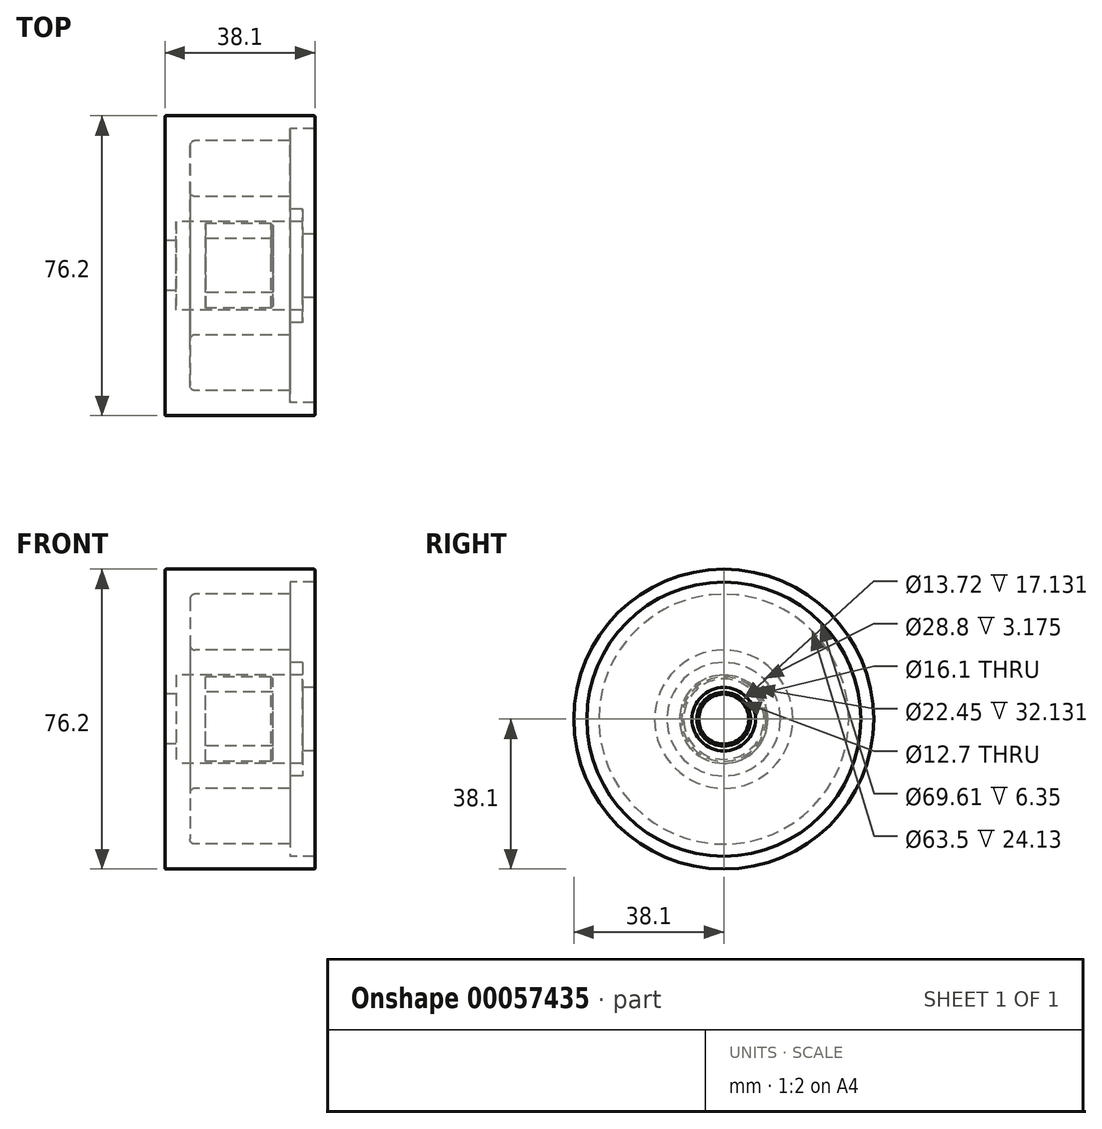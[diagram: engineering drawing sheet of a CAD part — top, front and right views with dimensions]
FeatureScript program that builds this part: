
annotation { "Feature Type Name" : "Feature", "Feature Type Description" : "" }
export const myFeature = defineFeature(function(context is Context, id is Id, definition is map)
    precondition{}
    {
        {
            var Q0;
            Q0=qCreatedBy(makeId("Front.planeOp"),FACE);
            var sketch = newSketch(context, id + "F0", { "sketchPlane" : qUnion([Q0])});
            skLineSegment(sketch, "E0.bottom", {"start": v(0.25, 38.1) * mm, "end": v(37.85, 38.1) * mm});
            skLineSegment(sketch, "E0.left", {"start": v(0, 37.85) * mm, "end": v(0, 6.35) * mm});
            skLineSegment(sketch, "E0.right", {"start": v(38.1, 37.85) * mm, "end": v(38.1, 31.77) * mm});
            skLineSegment(sketch, "E1.bottom", {"start": v(31.75, 31.75) * mm, "end": v(7.62, 31.75) * mm});
            skLineSegment(sketch, "E1.top", {"start": v(31.75, 17.58) * mm, "end": v(7.62, 17.58) * mm});
            skLineSegment(sketch, "E1.right", {"start": v(6.35, 30.48) * mm, "end": v(6.35, 18.85) * mm});
            skLineSegment(sketch, "E2.trimOffspring", {"start": v(38.1, 17.58) * mm, "end": v(38.1, 11.23) * mm});
            skLineSegment(sketch, "E3.bottom", {"start": v(0, 6.35) * mm, "end": v(2.8, 6.35) * mm});
            skLineSegment(sketch, "E4.bottom", {"start": v(38.1, 11.23) * mm, "end": v(2.8, 11.23) * mm});
            skLineSegment(sketch, "E4.right", {"start": v(2.8, 11.23) * mm, "end": v(2.8, 6.35) * mm});
            skPoint(sketch, "E5.visualSharp", {"position": v(0, 38.1) * mm});
            skArc(sketch, "E5.filletArc", {"start": v(0.25, 38.1) * mm, "mid": v(0.07, 38.03) * mm, "end": v(0, 37.85) * mm});
            skPoint(sketch, "E6.visualSharp", {"position": v(38.1, 38.1) * mm});
            skArc(sketch, "E6.filletArc", {"start": v(38.1, 37.85) * mm, "mid": v(38.03, 38.03) * mm, "end": v(37.85, 38.1) * mm});
            skPoint(sketch, "E7.visualSharp", {"position": v(38.1, 31.75) * mm});
            skPoint(sketch, "E8.visualSharp", {"position": v(6.35, 31.75) * mm});
            skArc(sketch, "E8.filletArc", {"start": v(7.62, 31.75) * mm, "mid": v(6.72, 31.38) * mm, "end": v(6.35, 30.48) * mm});
            skPoint(sketch, "E9.visualSharp", {"position": v(6.35, 17.58) * mm});
            skArc(sketch, "E9.filletArc", {"start": v(6.35, 18.85) * mm, "mid": v(6.72, 17.95) * mm, "end": v(7.62, 17.58) * mm});
            skPoint(sketch, "E10.visualSharp", {"position": v(38.1, 17.58) * mm});
            skLineSegment(sketch, "E11", {"start": v(0, 0) * mm, "end": v(46.74, 0) * mm, "construction": true});
            skLineSegment(sketch, "E12.left", {"start": v(38.1, 31.77) * mm, "end": v(38.1, 17.46) * mm});
            skLineSegment(sketch, "E12.right", {"start": v(31.75, 31.75) * mm, "end": v(31.75, 17.58) * mm});
            skPoint(sketch, "E13.visualSharp", {"position": v(31.75, 17.58) * mm});
            skSolve(sketch);
        }
        {
            var Q0;
            Q0=makeQuery(id+"F0.imprint","IMPRINT",FACE,{"disambiguationData":[TD([[makeQuery(id+"F0.imprint","IMPRINT",EDGE,{"derivedFrom":sQuery(id+"F0.wireOp",EDGE,"E0.bottom")}),-1.0]])]});
            var Q1;
            Q1=sQuery(id+"F0.wireOp",EDGE,"E11");
            revolve(context, id + "F1", {"entities" : qUnion([Q0]), "axis" : qUnion([Q1]), "revolveType" : RevolveType.FULL});
        }
        {
            var Q0;
            Q0=qCreatedBy(makeId("Front.planeOp"),FACE);
            var sketch = newSketch(context, id + "F2", { "sketchPlane" : qUnion([Q0])});
            skLineSegment(sketch, "E14.0", {"start": v(38.1, 37.85) * mm, "end": v(38.1, 31.77) * mm, "construction": true});
            skLineSegment(sketch, "E15.0", {"start": v(31.75, 31.75) * mm, "end": v(31.75, 17.58) * mm, "construction": true});
            skLineSegment(sketch, "E16.0", {"start": v(38.1, 17.58) * mm, "end": v(38.1, 11.23) * mm, "construction": true});
            skLineSegment(sketch, "E17.bottom", {"start": v(38.1, 34.8) * mm, "end": v(31.75, 34.8) * mm});
            skLineSegment(sketch, "E17.top", {"start": v(34.93, 14.4) * mm, "end": v(31.75, 14.4) * mm});
            skLineSegment(sketch, "E17.left", {"start": v(38.1, 34.8) * mm, "end": v(38.1, 14.4) * mm});
            skLineSegment(sketch, "E17.right", {"start": v(31.75, 34.8) * mm, "end": v(31.75, 14.4) * mm});
            skLineSegment(sketch, "E18.top", {"start": v(38.1, 8.05) * mm, "end": v(34.93, 8.05) * mm});
            skLineSegment(sketch, "E18.left", {"start": v(38.1, 11.23) * mm, "end": v(38.1, 8.05) * mm});
            skLineSegment(sketch, "E18.right", {"start": v(34.93, 14.4) * mm, "end": v(34.93, 8.05) * mm});
            skLineSegment(sketch, "E19", {"start": v(38.1, 14.4) * mm, "end": v(38.1, 11.23) * mm});
            skSolve(sketch);
        }
        {
            var Q0;
            Q0 = qSketchRegion(id + "F2", true);
            var Q1;
            Q1=sQuery(id+"F0.wireOp",EDGE,"E11");
            revolve(context, id + "F3", {"entities" : qUnion([Q0]), "axis" : qUnion([Q1]), "revolveType" : RevolveType.FULL});
        }
        {
            var Q0;
            Q0=makeQuery(id+"F1.opRevolve","SWEPT_FACE",FACE,{"disambiguationData":[OSD([sQuery(id+"F0.wireOp",EDGE,"E4.right")])]});
            cPlane(context, id + "F4", {"entities" : qUnion([Q0]), "cplaneType" : CPlaneType.OFFSET, "offset" : 7.5 * mm, "width" : 152.4 * mm, "height" : 152.4 * mm});
        }
        {
            var Q0;
            Q0=makeQuery(id+"F3.opRevolve","SWEPT_BODY",BODY,{"disambiguationData":[OSD([sQuery(id+"F2.wireOp",EDGE,"E17.bottom"),sQuery(id+"F2.wireOp",EDGE,"E17.top"),sQuery(id+"F2.wireOp",EDGE,"E17.left"),sQuery(id+"F2.wireOp",EDGE,"E17.right")])]});
            var Q1;
            Q1=makeQuery(id+"F1.opRevolve","SWEPT_BODY",BODY,{"disambiguationData":[OSD([sQuery(id+"F0.wireOp",EDGE,"E0.bottom"),sQuery(id+"F0.wireOp",EDGE,"E0.left"),sQuery(id+"F0.wireOp",EDGE,"E0.right"),sQuery(id+"F0.wireOp",EDGE,"E1.bottom"),sQuery(id+"F0.wireOp",EDGE,"E1.top"),sQuery(id+"F0.wireOp",EDGE,"E1.right"),sQuery(id+"F0.wireOp",EDGE,"E2.trimOffspring"),sQuery(id+"F0.wireOp",EDGE,"E3.bottom"),sQuery(id+"F0.wireOp",EDGE,"E4.bottom"),sQuery(id+"F0.wireOp",EDGE,"E4.right"),sQuery(id+"F0.wireOp",EDGE,"E5.filletArc"),sQuery(id+"F0.wireOp",EDGE,"E6.filletArc"),sQuery(id+"F0.wireOp",EDGE,"E8.filletArc"),sQuery(id+"F0.wireOp",EDGE,"E9.filletArc"),sQuery(id+"F0.wireOp",EDGE,"E12.left"),sQuery(id+"F0.wireOp",EDGE,"E12.right"),sQuery(id+"F0.wireOp",EDGE,"deba94b6-71f0-4198-8a2f-3d76bc40c265.filletArc"),sQuery(id+"F0.wireOp",EDGE,"E13.filletArc")])]});
            booleanBodies(context, id + "F5", {"operationType" : BooleanOperationType.SUBTRACTION, "tools" : qUnion([Q0]), "targets" : qUnion([Q1]), "keepTools" : true});
        }
        {
            var Q0;
            Q0=qCreatedBy(id+"F4.planeOp",FACE);
            var sketch = newSketch(context, id + "F6", { "sketchPlane" : qUnion([Q0])});
            skCircle(sketch, "E20", {"center": v(0, 0) * mm, "radius": 10.72 * mm});
            skCircle(sketch, "E21", {"center": v(0, 0) * mm, "radius": 6.86 * mm});
            skCircle(sketch, "E22.0", {"center": v(0, 0) * mm, "radius": 11.23 * mm, "construction": true});
            skCircle(sketch, "E23.0", {"center": v(0, 0) * mm, "radius": 6.35 * mm, "construction": true});
            skSolve(sketch);
        }
        {
            var Q0;
            Q0=makeQuery(id+"F5.opBoolean","COPY",FACE,{"derivedFrom":makeQuery(id+"F3.opRevolve","SWEPT_FACE",FACE,{"disambiguationData":[OSD([sQuery(id+"F2.wireOp",EDGE,"E18.right")])]})});
            cPlane(context, id + "F7", {"entities" : qUnion([Q0]), "cplaneType" : CPlaneType.OFFSET, "offset" : 7.5 * mm, "oppositeDirection" : true, "width" : 152.4 * mm, "height" : 152.4 * mm});
        }
        {
            var Q0;
            Q0 = qSketchRegion(id + "F6", true);
            var Q1;
            Q1=qCreatedBy(id+"F7.planeOp",FACE);
            extrude(context, id + "F8", {"entities" : qUnion([Q0]), "endBound" : BoundingType.UP_TO_SURFACE, "endBoundEntityFace" : qUnion([Q1]), "depth" : 25.4 * mm});
        }
        {
            var Q0;
            Q0=makeQuery(id+"F8.opExtrude","CAP_EDGE",EDGE,{"disambiguationData":[OSD([sQuery(id+"F6.wireOp",EDGE,"E20")])],"isStart":false});
            chamfer(context, id + "F9", {"entities" : qUnion([Q0]), "width" : 0.5 * mm, "tangentPropagation" : true});
        }
    });
